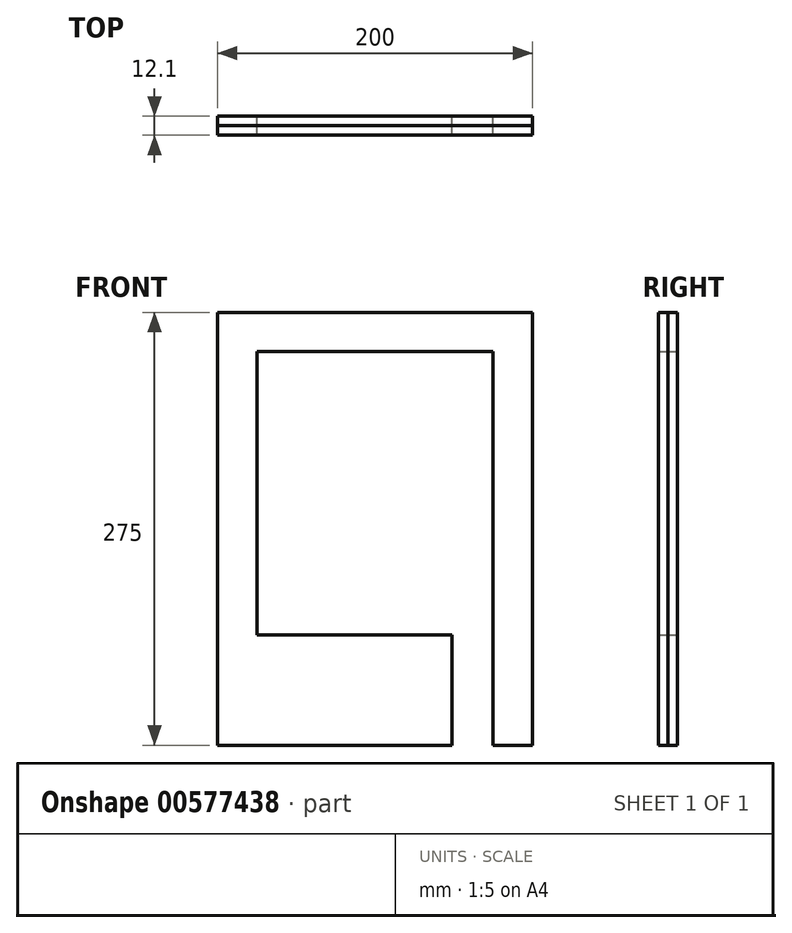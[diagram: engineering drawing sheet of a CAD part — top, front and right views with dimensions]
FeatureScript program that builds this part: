
annotation { "Feature Type Name" : "Feature", "Feature Type Description" : "" }
export const myFeature = defineFeature(function(context is Context, id is Id, definition is map)
    precondition{}
    {
        {
            var Q0;
            Q0=qCreatedBy(makeId("Front.planeOp"),FACE);
            var sketch = newSketch(context, id + "F0", { "sketchPlane" : qUnion([Q0])});
            skLineSegment(sketch, "E0.bottom", {"start": v(0, 0) * mm, "end": v(200, 0) * mm});
            skLineSegment(sketch, "E0.top", {"start": v(0, 275) * mm, "end": v(200, 275) * mm});
            skLineSegment(sketch, "E0.left", {"start": v(0, 0) * mm, "end": v(0, 275) * mm});
            skLineSegment(sketch, "E0.right", {"start": v(200, 0) * mm, "end": v(200, 275) * mm});
            skLineSegment(sketch, "E1.bottom", {"start": v(25, 250) * mm, "end": v(175, 250) * mm});
            skLineSegment(sketch, "E1.top", {"start": v(25, 70) * mm, "end": v(175, 70) * mm});
            skLineSegment(sketch, "E1.left", {"start": v(25, 250) * mm, "end": v(25, 70) * mm});
            skLineSegment(sketch, "E1.right", {"start": v(175, 250) * mm, "end": v(175, 70) * mm});
            skLineSegment(sketch, "E2.bottom", {"start": v(175, 70) * mm, "end": v(149, 70) * mm});
            skLineSegment(sketch, "E2.top", {"start": v(175, 0) * mm, "end": v(149, 0) * mm});
            skLineSegment(sketch, "E2.left", {"start": v(175, 70) * mm, "end": v(175, 0) * mm});
            skLineSegment(sketch, "E2.right", {"start": v(149, 70) * mm, "end": v(149, 0) * mm});
            skSolve(sketch);
        }
        {
            var Q0;
            Q0=makeQuery(id+"F0.imprint","IMPRINT",FACE,{"disambiguationData":[TD([[makeQuery(id+"F0.imprint","IMPRINT",EDGE,{"derivedFrom":sQuery(id+"F0.wireOp",EDGE,"E0.top")}),-1.0]])]});
            extrude(context, id + "F1", {"entities" : qUnion([Q0]), "depth" : 6 * mm, "offsetDistance" : 25 * mm});
        }
        {
            var Q0;
            Q0=makeQuery(id+"F1.opExtrude","CAP_FACE",FACE,{"disambiguationData":[OSD([sQuery(id+"F0.wireOp",EDGE,"E0.bottom"),sQuery(id+"F0.wireOp",EDGE,"E0.top"),sQuery(id+"F0.wireOp",EDGE,"E0.left"),sQuery(id+"F0.wireOp",EDGE,"E0.right"),sQuery(id+"F0.wireOp",EDGE,"E1.bottom"),sQuery(id+"F0.wireOp",EDGE,"E1.top"),sQuery(id+"F0.wireOp",EDGE,"E1.left"),sQuery(id+"F0.wireOp",EDGE,"E1.right"),sQuery(id+"F0.wireOp",EDGE,"E2.left"),sQuery(id+"F0.wireOp",EDGE,"E2.right")])],"isStart":false});
            extrude(context, id + "F2", {"entities" : qUnion([Q0]), "operationType" : NewBodyOperationType.ADD, "depth" : 6.1 * mm, "offsetDistance" : 25 * mm, "hasSecondDirection" : true, "secondDirectionOppositeDirection" : false, "secondDirectionDepth" : 0.1 * mm});
        }
    });
